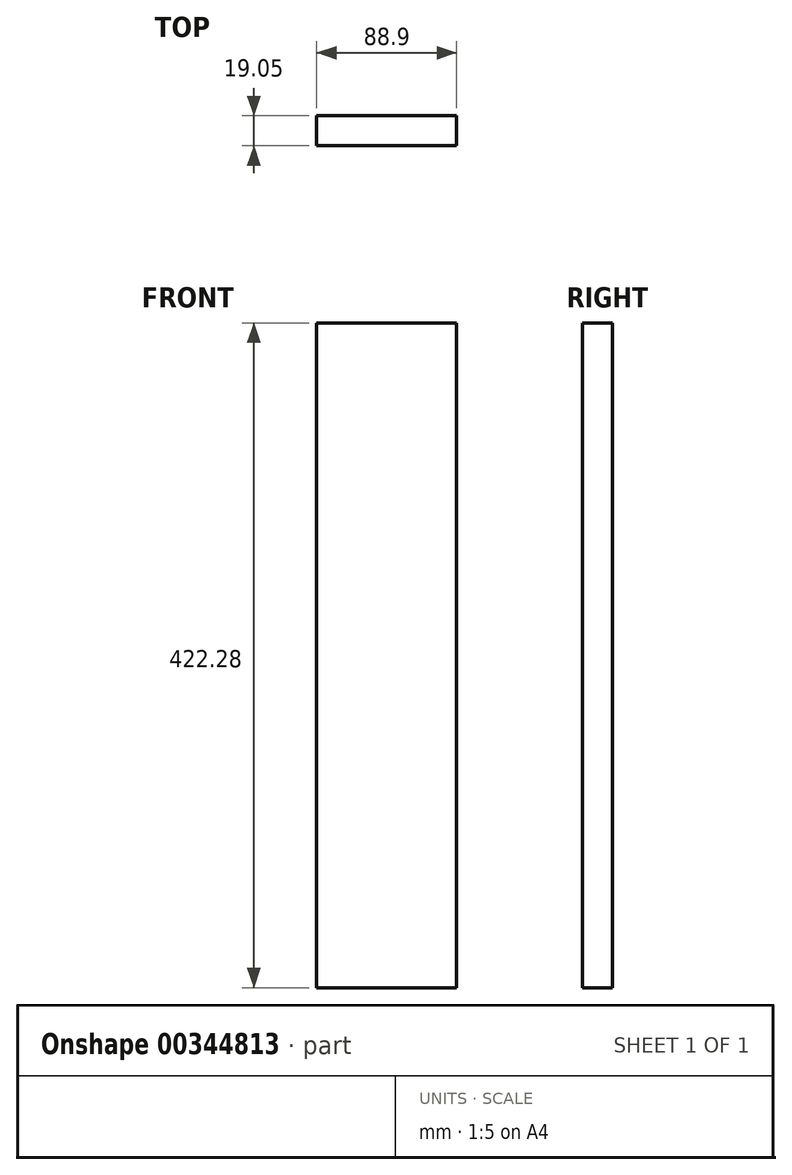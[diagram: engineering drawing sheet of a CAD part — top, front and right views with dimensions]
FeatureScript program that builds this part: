
annotation { "Feature Type Name" : "Feature", "Feature Type Description" : "" }
export const myFeature = defineFeature(function(context is Context, id is Id, definition is map)
    precondition{}
    {
        {
            var Q0;
            Q0=qCreatedBy(makeId("Top.planeOp"),FACE);
            var sketch = newSketch(context, id + "F0", { "sketchPlane" : qUnion([Q0])});
            skLineSegment(sketch, "E0.bottom", {"start": v(0, 0) * mm, "end": v(88.9, 0) * mm});
            skLineSegment(sketch, "E0.top", {"start": v(0, 19.05) * mm, "end": v(88.9, 19.05) * mm});
            skLineSegment(sketch, "E0.left", {"start": v(0, 0) * mm, "end": v(0, 19.05) * mm});
            skLineSegment(sketch, "E0.right", {"start": v(88.9, 0) * mm, "end": v(88.9, 19.05) * mm});
            skSolve(sketch);
        }
        {
            var Q0;
            Q0=makeQuery(id+"F0.imprint","IMPRINT",FACE,{"disambiguationData":[TD([[makeQuery(id+"F0.imprint","IMPRINT",EDGE,{"derivedFrom":sQuery(id+"F0.wireOp",EDGE,"E0.bottom")}),1.0]])]});
            extrude(context, id + "F1", {"entities" : qUnion([Q0]), "depth" : 422.27 * mm});
        }
    });
